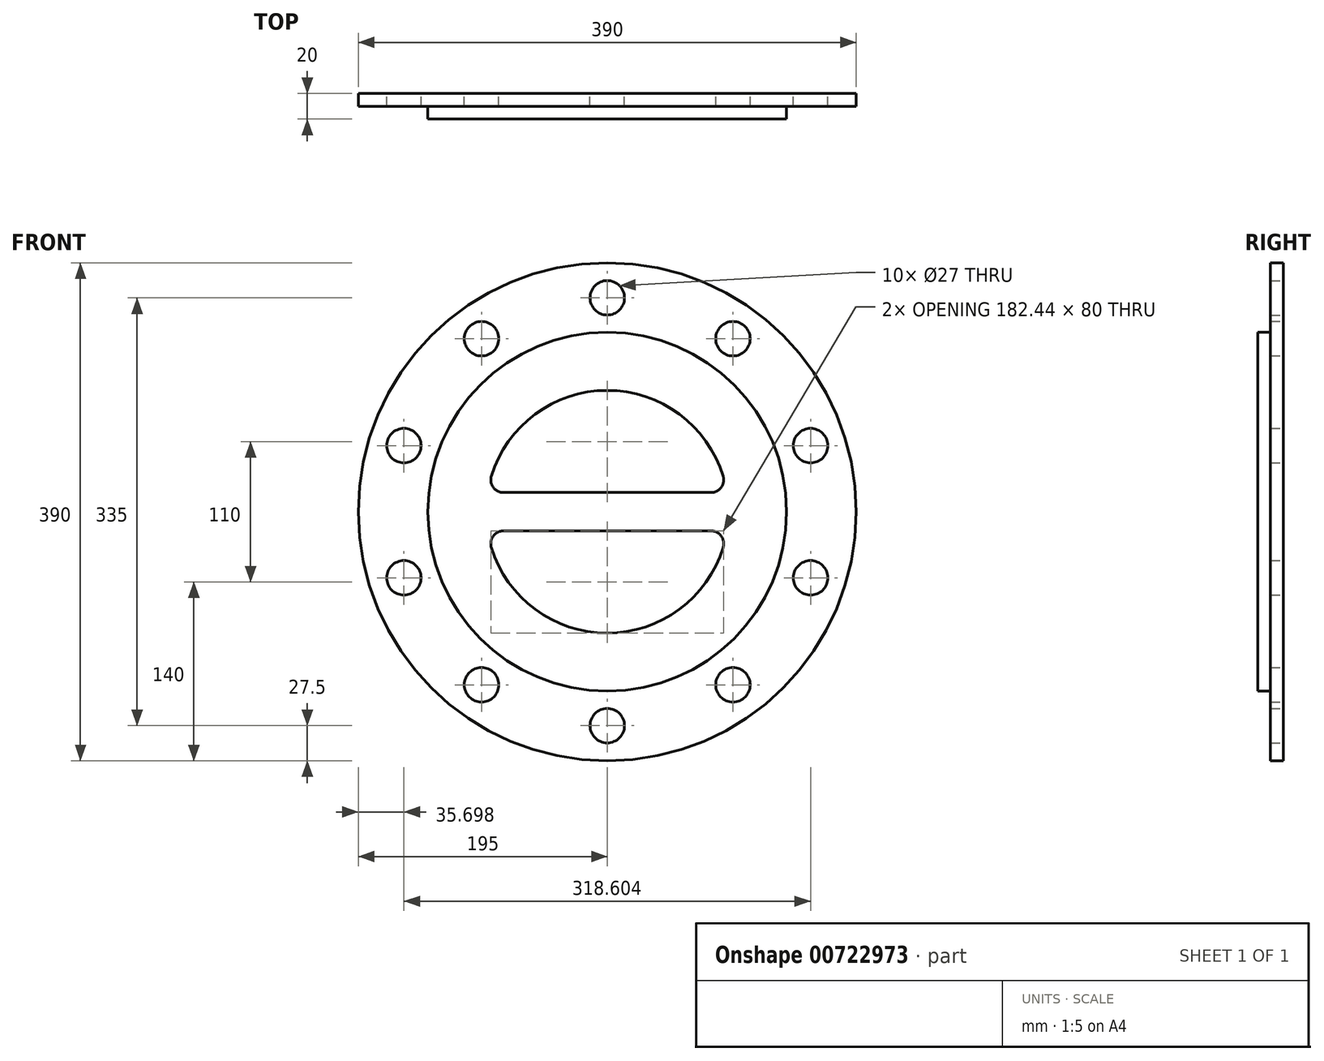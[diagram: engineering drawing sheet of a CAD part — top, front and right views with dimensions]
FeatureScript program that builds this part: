
annotation { "Feature Type Name" : "Feature", "Feature Type Description" : "" }
export const myFeature = defineFeature(function(context is Context, id is Id, definition is map)
    precondition{}
    {
        {
            var Q0;
            Q0=qCreatedBy(makeId("Front.planeOp"),FACE);
            var sketch = newSketch(context, id + "F0", { "sketchPlane" : qUnion([Q0])});
            skCircle(sketch, "E0", {"center": v(0, 0) * mm, "radius": 195 * mm});
            skCircle(sketch, "E1", {"center": v(0, 167.5) * mm, "radius": 13.5 * mm});
            skCircle(sketch, "E2.1.0", {"center": v(-98.45, 135.51) * mm, "radius": 13.5 * mm});
            skCircle(sketch, "E2.2.0", {"center": v(-159.3, 51.76) * mm, "radius": 13.5 * mm});
            skCircle(sketch, "E2.3.0", {"center": v(-159.3, -51.76) * mm, "radius": 13.5 * mm});
            skCircle(sketch, "E2.4.0", {"center": v(-98.45, -135.51) * mm, "radius": 13.5 * mm});
            skCircle(sketch, "E2.5.0", {"center": v(0, -167.5) * mm, "radius": 13.5 * mm});
            skCircle(sketch, "E2.6.0", {"center": v(98.45, -135.51) * mm, "radius": 13.5 * mm});
            skCircle(sketch, "E2.7.0", {"center": v(159.3, -51.76) * mm, "radius": 13.5 * mm});
            skCircle(sketch, "E2.8.0", {"center": v(159.3, 51.76) * mm, "radius": 13.5 * mm});
            skCircle(sketch, "E2.9.0", {"center": v(98.45, 135.51) * mm, "radius": 13.5 * mm});
            skCircle(sketch, "E3", {"center": v(0, 0) * mm, "radius": 140.5 * mm});
            skSolve(sketch);
        }
        {
            var Q0;
            Q0=makeQuery(id+"F0.imprint","IMPRINT",FACE,{"disambiguationData":[TD([[makeQuery(id+"F0.imprint","IMPRINT",EDGE,{"derivedFrom":sQuery(id+"F0.wireOp",EDGE,"E3")}),1.0]])]});
            extrude(context, id + "F1", {"entities" : qUnion([Q0]), "depth" : 20 * mm, "offsetDistance" : 25 * mm});
        }
        {
            var Q0;
            Q0 = qSketchRegion(id + "F0", true);
            extrude(context, id + "F2", {"entities" : qUnion([Q0]), "operationType" : NewBodyOperationType.ADD, "depth" : 10 * mm, "offsetDistance" : 25 * mm});
        }
        {
            var Q0;
            Q0=makeQuery(id+"F1.opExtrude","CAP_FACE",FACE,{"disambiguationData":[OSD([sQuery(id+"F0.wireOp",EDGE,"E3")])],"isStart":false});
            var sketch = newSketch(context, id + "F3", { "sketchPlane" : qUnion([Q0])});
            skArc(sketch, "E4", {"start": v(90.8, 27.94) * mm, "mid": v(0, 95) * mm, "end": v(-90.8, 27.94) * mm});
            skLineSegment(sketch, "E5", {"start": v(-81.24, 15) * mm, "end": v(81.24, 15) * mm});
            skLineSegment(sketch, "E6", {"start": v(-81.24, -15) * mm, "end": v(81.24, -15) * mm});
            skArc(sketch, "E7.trimOffspring", {"start": v(-90.8, -27.94) * mm, "mid": v(0, -95) * mm, "end": v(90.8, -27.94) * mm});
            skPoint(sketch, "E8.visualSharp", {"position": v(-93.8, 15) * mm});
            skArc(sketch, "E8.filletArc", {"start": v(-90.8, 27.94) * mm, "mid": v(-89.28, 19.06) * mm, "end": v(-81.24, 15) * mm});
            skPoint(sketch, "E9.visualSharp", {"position": v(93.8, 15) * mm});
            skArc(sketch, "E9.filletArc", {"start": v(81.24, 15) * mm, "mid": v(89.28, 19.06) * mm, "end": v(90.8, 27.94) * mm});
            skPoint(sketch, "E10.visualSharp", {"position": v(93.8, -15) * mm});
            skArc(sketch, "E10.filletArc", {"start": v(90.8, -27.94) * mm, "mid": v(89.28, -19.06) * mm, "end": v(81.24, -15) * mm});
            skPoint(sketch, "E11.visualSharp", {"position": v(-93.8, -15) * mm});
            skArc(sketch, "E11.filletArc", {"start": v(-81.24, -15) * mm, "mid": v(-89.28, -19.06) * mm, "end": v(-90.8, -27.94) * mm});
            skSolve(sketch);
        }
        {
            var Q0;
            Q0=makeQuery(id+"F3.imprint","IMPRINT",FACE,{"disambiguationData":[TD([[makeQuery(id+"F3.imprint","IMPRINT",EDGE,{"derivedFrom":sQuery(id+"F3.wireOp",EDGE,"E4")}),1.0]])]});
            var Q1;
            Q1=makeQuery(id+"F3.imprint","IMPRINT",FACE,{"disambiguationData":[TD([[makeQuery(id+"F3.imprint","IMPRINT",EDGE,{"derivedFrom":sQuery(id+"F3.wireOp",EDGE,"E6")}),-1.0]])]});
            extrude(context, id + "F4", {"entities" : qUnion([Q0, Q1]), "operationType" : NewBodyOperationType.REMOVE, "oppositeDirection" : true, "depth" : 25 * mm, "offsetDistance" : 25 * mm});
        }
    });
